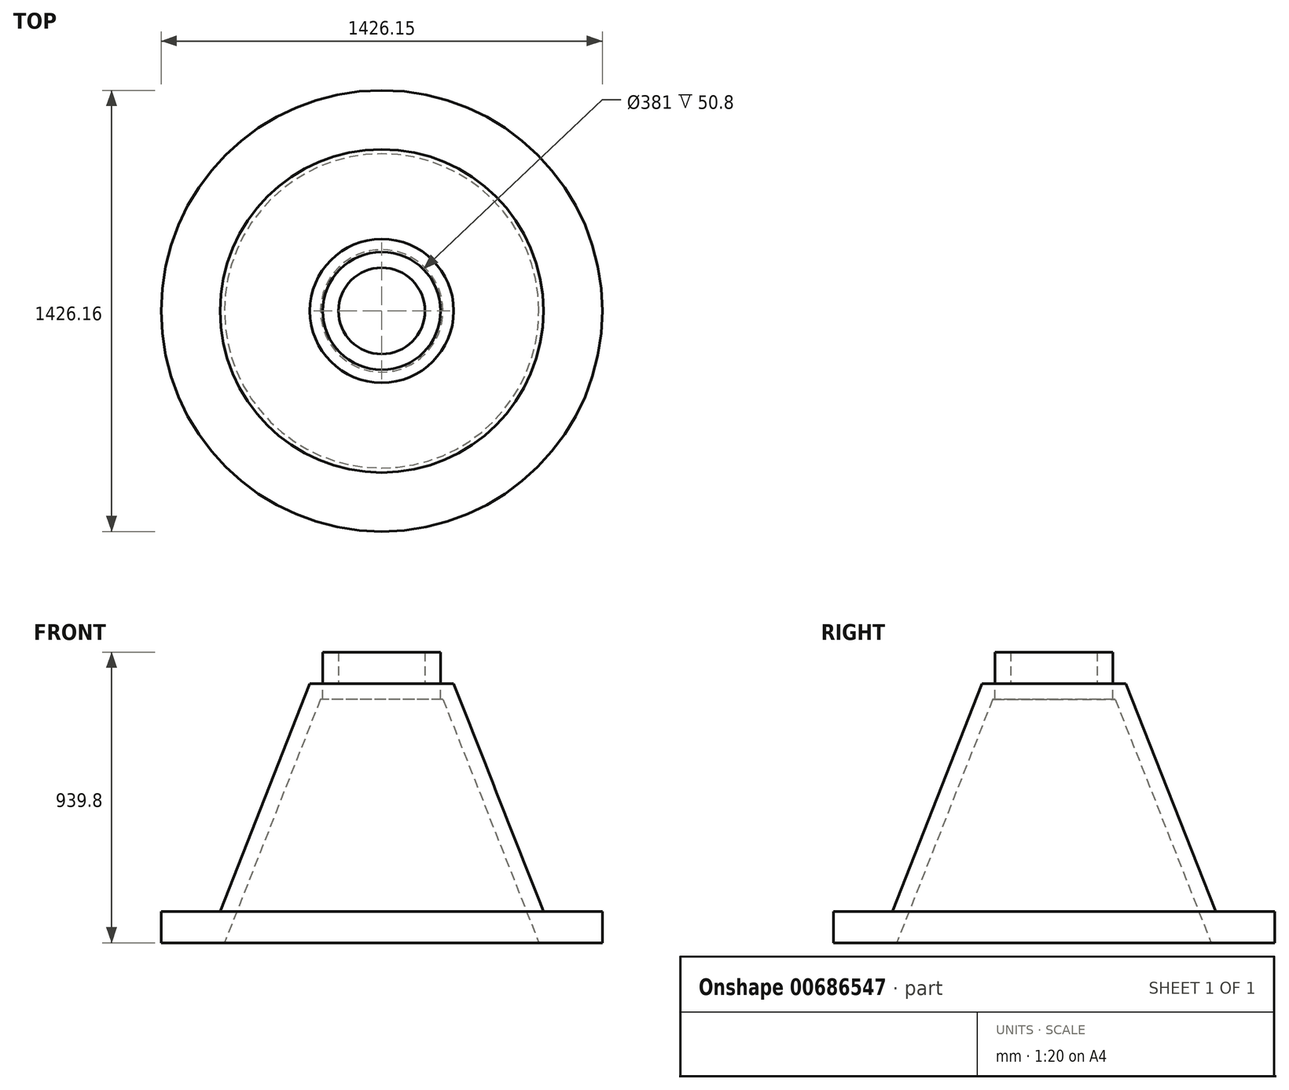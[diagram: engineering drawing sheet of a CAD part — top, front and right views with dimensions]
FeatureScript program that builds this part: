
annotation { "Feature Type Name" : "Feature", "Feature Type Description" : "" }
export const myFeature = defineFeature(function(context is Context, id is Id, definition is map)
    precondition{}
    {
        {
            var Q0;
            Q0=qCreatedBy(makeId("Front.planeOp"),FACE);
            var sketch = newSketch(context, id + "F0", { "sketchPlane" : qUnion([Q0])});
            skLineSegment(sketch, "E0", {"start": v(223.76, 597.4) * mm, "end": v(172.96, 597.4) * mm});
            skLineSegment(sketch, "E1", {"start": v(172.96, 597.4) * mm, "end": v(-117.2, -139.2) * mm});
            skLineSegment(sketch, "E2", {"start": v(-117.2, -139.2) * mm, "end": v(-307.7, -139.2) * mm});
            skLineSegment(sketch, "E3", {"start": v(-307.7, -139.2) * mm, "end": v(-307.7, -240.8) * mm});
            skLineSegment(sketch, "E4", {"start": v(-307.7, -240.8) * mm, "end": v(-102.61, -240.8) * mm});
            skLineSegment(sketch, "E5", {"start": v(-102.61, -240.8) * mm, "end": v(207.55, 546.6) * mm});
            skLineSegment(sketch, "E6", {"start": v(207.55, 546.6) * mm, "end": v(214.89, 546.6) * mm});
            skLineSegment(sketch, "E7", {"start": v(214.89, 546.6) * mm, "end": v(214.89, 648.2) * mm});
            skLineSegment(sketch, "E8", {"start": v(214.89, 648.2) * mm, "end": v(164.09, 648.2) * mm});
            skLineSegment(sketch, "E9", {"start": v(164.09, 648.2) * mm, "end": v(223.76, 597.4) * mm});
            skLineSegment(sketch, "E10", {"start": v(405.39, 733) * mm, "end": v(405.39, -462.25) * mm});
            skSolve(sketch);
        }
        {
            var Q0;
            {var subQ0=sQuery(id+"F0.wireOp",EDGE,"E0");Q0=makeQuery(id+"F0.imprint","IMPRINT",FACE,{"disambiguationData":[TD([[makeQuery(id+"F0.imprint","IMPRINT",EDGE,{"derivedFrom":subQ0}),1.0]])]});}
            var Q1;
            Q1=sQuery(id+"F0.wireOp",EDGE,"E10");
            revolve(context, id + "F1", {"entities" : qUnion([Q0]), "axis" : qUnion([Q1]), "revolveType" : RevolveType.FULL});
        }
        {
            var Q0;
            Q0=makeQuery(id+"F1.opRevolve","SWEPT_FACE",FACE,{"disambiguationData":[OSD([sQuery(id+"F0.wireOp",EDGE,"E0")])]});
            var sketch = newSketch(context, id + "F2", { "sketchPlane" : qUnion([Q0])});
            skCircle(sketch, "E11", {"center": v(405.39, 0) * mm, "radius": 139.7 * mm});
            skCircle(sketch, "E12", {"center": v(405.39, 0) * mm, "radius": 190.5 * mm});
            skSolve(sketch);
        }
        {
            var Q0;
            Q0 = qSketchRegion(id + "F2", true);
            extrude(context, id + "F3", {"entities" : qUnion([Q0]), "depth" : 101.6 * mm, "offsetDistance" : 25.4 * mm});
        }
    });
